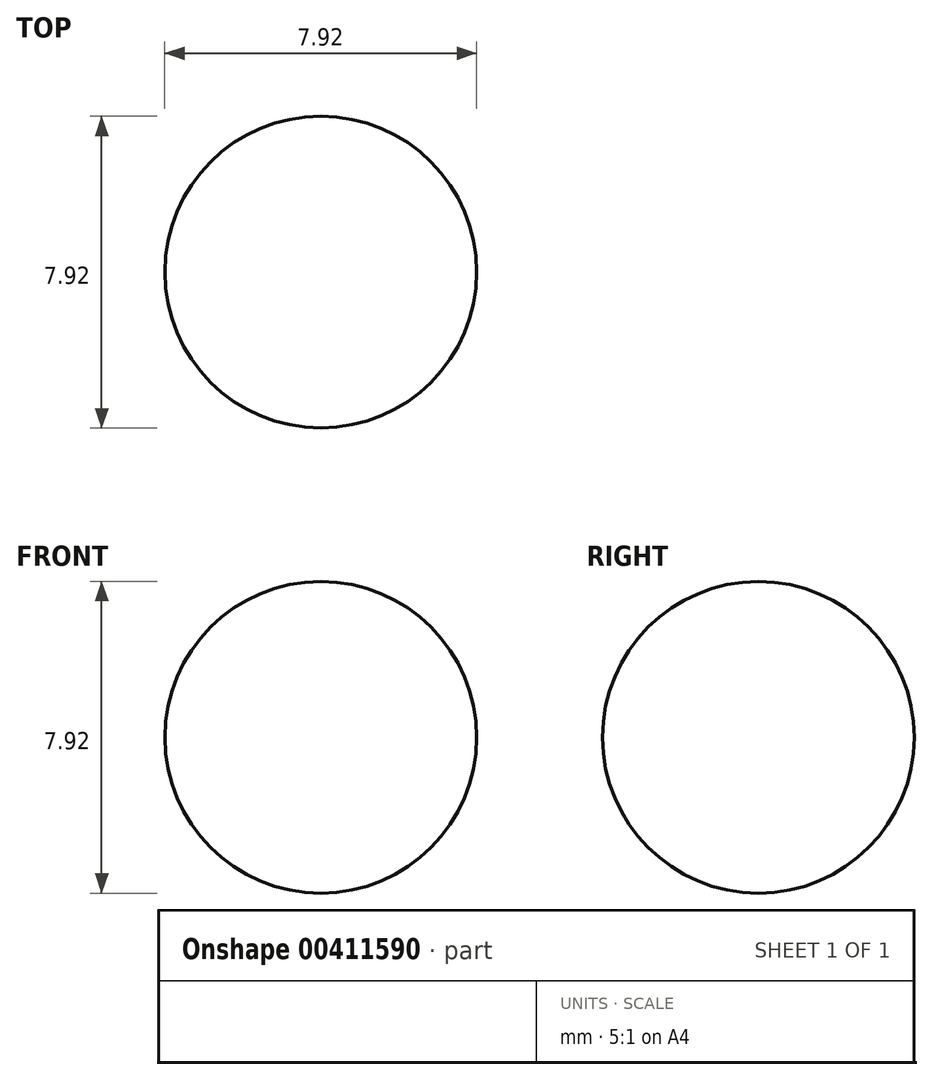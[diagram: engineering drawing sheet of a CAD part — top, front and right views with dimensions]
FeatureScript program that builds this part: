
annotation { "Feature Type Name" : "Feature", "Feature Type Description" : "" }
export const myFeature = defineFeature(function(context is Context, id is Id, definition is map)
    precondition{}
    {
        {
            var Q0;
            Q0=qCreatedBy(makeId("Top.planeOp"),FACE);
            var sketch = newSketch(context, id + "F0", { "sketchPlane" : qUnion([Q0])});
            skLineSegment(sketch, "E0", {"start": v(-1.19, 8.22) * mm, "end": v(6.73, 8.22) * mm});
            skCircle(sketch, "E1", {"center": v(2.77, 8.22) * mm, "radius": 3.96 * mm});
            skSolve(sketch);
        }
        {
            var Q0;
            {var subQ0=sQuery(id+"F0.wireOp",EDGE,"E0");Q0=makeQuery(id+"F0.imprint","IMPRINT",FACE,{"disambiguationData":[TD([[makeQuery(id+"F0.imprint","IMPRINT",EDGE,{"derivedFrom":subQ0}),1.0]])]});}
            var Q1;
            Q1=sQuery(id+"F0.wireOp",EDGE,"E0");
            revolve(context, id + "F1", {"entities" : qUnion([Q0]), "axis" : qUnion([Q1]), "revolveType" : RevolveType.FULL});
        }
    });
